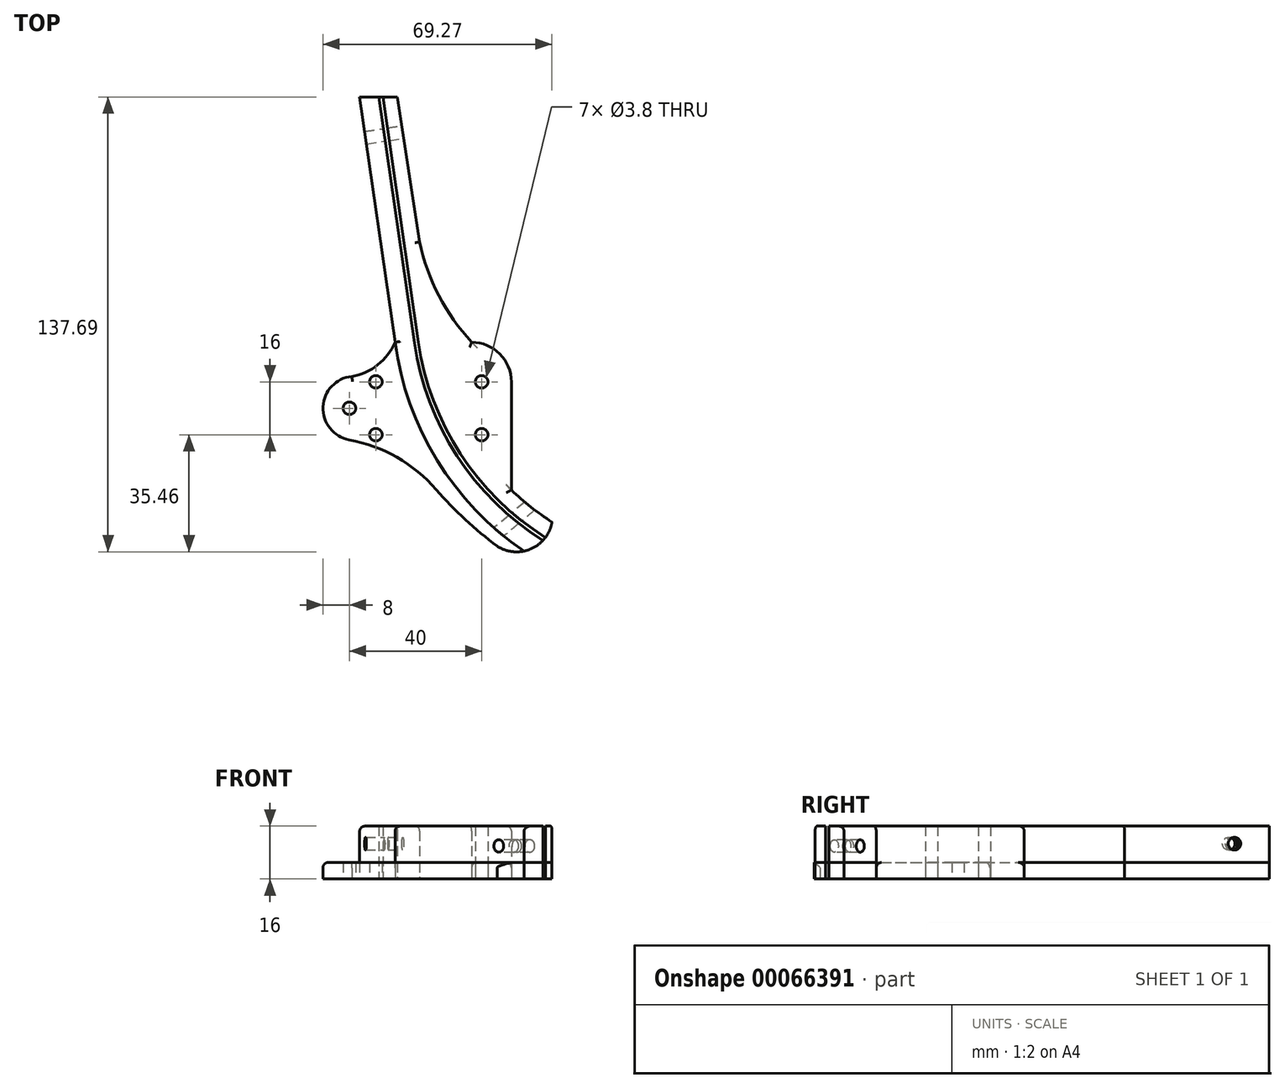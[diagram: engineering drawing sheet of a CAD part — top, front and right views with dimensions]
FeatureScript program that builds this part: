
annotation { "Feature Type Name" : "Feature", "Feature Type Description" : "" }
export const myFeature = defineFeature(function(context is Context, id is Id, definition is map)
    precondition{}
    {
        {
            var Q0;
            Q0=qCreatedBy(makeId("Top.planeOp"),FACE);
            var sketch = newSketch(context, id + "F0", { "sketchPlane" : qUnion([Q0])});
            skLineSegment(sketch, "E0.rect.top", {"start": v(6.92, 32.4) * mm, "end": v(18, 32.4) * mm});
            skLineSegment(sketch, "E0.rect.right", {"start": v(30, -30.94) * mm, "end": v(30, 20.4) * mm});
            skPoint(sketch, "E0.rect.middle", {"position": v(0, 0) * mm});
            skLineSegment(sketch, "E1", {"start": v(0, -32.4) * mm, "end": v(0, -38.4) * mm, "construction": true});
            skPoint(sketch, "E1.endSnap0", {"position": v(0, -32.4) * mm});
            skPoint(sketch, "E2.center", {"position": v(0, 12.4) * mm});
            skLineSegment(sketch, "E3.direction1", {"start": v(8, 12.4) * mm, "end": v(40, 12.4) * mm, "construction": true});
            skLineSegment(sketch, "E4", {"start": v(0, 12.4) * mm, "end": v(85, 12.4) * mm, "construction": true});
            skLineSegment(sketch, "E5", {"start": v(85, 12.4) * mm, "end": v(85, 44.4) * mm, "construction": true});
            skLineSegment(sketch, "E6", {"start": v(0, 12.4) * mm, "end": v(0, 32.4) * mm, "construction": true});
            skLineSegment(sketch, "E7", {"start": v(0, 12.4) * mm, "end": v(0, -32.4) * mm, "construction": true});
            skCircle(sketch, "E8", {"center": v(85, 44.4) * mm, "radius": 11.1 * mm, "construction": true});
            skCircle(sketch, "E9", {"center": v(85, 44.4) * mm, "radius": 80 * mm, "construction": true});
            skArc(sketch, "E10.0", {"start": v(1.86, 32.4) * mm, "mid": v(14.57, -1.37) * mm, "end": v(40.27, -26.7) * mm});
            skArc(sketch, "E11.0", {"start": v(-5.2, 32.4) * mm, "mid": v(7.55, -3.38) * mm, "end": v(33.8, -30.83) * mm});
            skArc(sketch, "E12.0", {"start": v(6.92, 32.4) * mm, "mid": v(18.74, 1.38) * mm, "end": v(42.27, -22.05) * mm});
            skArc(sketch, "E13", {"start": v(-18.28, 22.06) * mm, "mid": v(-27, 12.81) * mm, "end": v(-19.1, 2.86) * mm});
            skArc(sketch, "E14", {"start": v(7.25, -12.26) * mm, "mid": v(16.03, -21.28) * mm, "end": v(25.7, -29.33) * mm});
            skPoint(sketch, "E15.orphan", {"position": v(-30, 32.4) * mm});
            skPoint(sketch, "E16.orphan", {"position": v(-30, -32.4) * mm});
            skLineSegment(sketch, "E17.bottom", {"start": v(30, 32.4) * mm, "end": v(18, 32.4) * mm, "construction": true});
            skLineSegment(sketch, "E17.top", {"start": v(30, 20.4) * mm, "end": v(18, 20.4) * mm, "construction": true});
            skLineSegment(sketch, "E17.left", {"start": v(30, 32.4) * mm, "end": v(30, 20.4) * mm, "construction": true});
            skLineSegment(sketch, "E17.right", {"start": v(18, 32.4) * mm, "end": v(18, 20.4) * mm, "construction": true});
            skArc(sketch, "E18.trimOffspring", {"start": v(30, 20.4) * mm, "mid": v(26.49, 28.89) * mm, "end": v(18, 32.4) * mm});
            skLineSegment(sketch, "E19", {"start": v(85, 12.4) * mm, "end": v(21, 12.4) * mm, "construction": true});
            skLineSegment(sketch, "E20", {"start": v(21, 12.4) * mm, "end": v(21, 20.4) * mm, "construction": true});
            skCircle(sketch, "E21", {"center": v(21, 20.4) * mm, "radius": 1.9 * mm});
            skLineSegment(sketch, "E22", {"start": v(21, 12.4) * mm, "end": v(21, 4.4) * mm, "construction": true});
            skCircle(sketch, "E23", {"center": v(21, 4.4) * mm, "radius": 1.9 * mm});
            skLineSegment(sketch, "E24", {"start": v(21, 12.4) * mm, "end": v(-19, 12.4) * mm, "construction": true});
            skCircle(sketch, "E25", {"center": v(-19, 12.4) * mm, "radius": 1.9 * mm});
            skArc(sketch, "E26", {"start": v(-18.28, 22.06) * mm, "mid": v(-10.43, 25.57) * mm, "end": v(-5.2, 32.4) * mm});
            skArc(sketch, "E27", {"start": v(7.25, -12.26) * mm, "mid": v(-4.62, -2.44) * mm, "end": v(-19.1, 2.86) * mm});
            skLineSegment(sketch, "E28", {"start": v(-11, 12.4) * mm, "end": v(-11, 20.4) * mm, "construction": true});
            skCircle(sketch, "E29", {"center": v(-11, 20.4) * mm, "radius": 1.9 * mm});
            skLineSegment(sketch, "E30", {"start": v(-11, 12.4) * mm, "end": v(-11, 4.4) * mm, "construction": true});
            skCircle(sketch, "E31", {"center": v(-11, 4.4) * mm, "radius": 1.9 * mm});
            skArc(sketch, "E32.0", {"start": v(0.67, 32.23) * mm, "mid": v(13.52, -1.96) * mm, "end": v(39.5, -27.63) * mm});
            skLineSegment(sketch, "E33", {"start": v(0.67, 32.23) * mm, "end": v(0.65, 32.4) * mm});
            skArc(sketch, "E34", {"start": v(25.7, -29.33) * mm, "mid": v(35.94, -30.14) * mm, "end": v(42.27, -22.05) * mm});
            skPoint(sketch, "E35.orphan", {"position": v(30, -32.4) * mm});
            skLineSegment(sketch, "E36", {"start": v(6.92, 32.4) * mm, "end": v(-4.48, 106.53) * mm});
            skLineSegment(sketch, "E37", {"start": v(-5.2, 32.4) * mm, "end": v(-15.92, 106.63) * mm});
            skLineSegment(sketch, "E38", {"start": v(-15.92, 106.63) * mm, "end": v(-4.48, 106.53) * mm});
            skLineSegment(sketch, "E39", {"start": v(0.67, 32.23) * mm, "end": v(-10.06, 106.58) * mm});
            skLineSegment(sketch, "E40", {"start": v(1.86, 32.4) * mm, "end": v(-8.84, 106.57) * mm});
            skArc(sketch, "E41", {"start": v(2.25, 62.76) * mm, "mid": v(8.06, 46.5) * mm, "end": v(18, 32.4) * mm});
            skSolve(sketch);
        }
        {
            var Q0;
            {var subQ0=sQuery(id+"F0.wireOp",EDGE,"E11.0");var subQ5=sQuery(id+"F0.wireOp",EDGE,"E0.rect.right");var subQ6=makeQuery(id+"F0.imprint","INTERSECT",VERTEX,{"derivedFrom":[subQ5,subQ0]});Q0=makeQuery(id+"F0.imprint","IMPRINT",FACE,{"disambiguationData":[TD([[makeQuery(id+"F0.imprint","IMPRINT",EDGE,{"disambiguationData":[TD([[subQ6,-1.0]])],"derivedFrom":subQ5}),1.0]])]});}
            var Q1;
            {var subQ0=sQuery(id+"F0.wireOp",EDGE,"E10.0");var subQ1=sQuery(id+"F0.wireOp",EDGE,"E0.rect.top");var subQ2=makeQuery(id+"F0.imprint","INTERSECT",VERTEX,{"derivedFrom":[subQ1,subQ0]});Q1=makeQuery(id+"F0.imprint","IMPRINT",FACE,{"disambiguationData":[TD([[makeQuery(id+"F0.imprint","IMPRINT",EDGE,{"disambiguationData":[TD([[subQ2,-1.0]])],"derivedFrom":subQ1}),-1.0]])]});}
            var Q2;
            {var subQ0=sQuery(id+"F0.wireOp",EDGE,"E12.0");var subQ1=sQuery(id+"F0.wireOp",EDGE,"E0.rect.right");var subQ2=makeQuery(id+"F0.imprint","INTERSECT",VERTEX,{"derivedFrom":[subQ1,subQ0]});Q2=makeQuery(id+"F0.imprint","IMPRINT",FACE,{"disambiguationData":[TD([[makeQuery(id+"F0.imprint","IMPRINT",EDGE,{"disambiguationData":[TD([[subQ2,1.0]])],"derivedFrom":subQ1}),-1.0]])]});}
            var Q3;
            {var subQ0=sQuery(id+"F0.wireOp",EDGE,"E11.0");var subQ1=sQuery(id+"F0.wireOp",EDGE,"E0.rect.right");var subQ2=makeQuery(id+"F0.imprint","INTERSECT",VERTEX,{"derivedFrom":[subQ1,subQ0]});Q3=makeQuery(id+"F0.imprint","IMPRINT",FACE,{"disambiguationData":[TD([[makeQuery(id+"F0.imprint","IMPRINT",EDGE,{"disambiguationData":[TD([[subQ2,-1.0]])],"derivedFrom":subQ1}),-1.0]])]});}
            var Q4;
            {var subQ0=sQuery(id+"F0.wireOp",EDGE,"E36");Q4=makeQuery(id+"F0.imprint","IMPRINT",FACE,{"disambiguationData":[TD([[makeQuery(id+"F0.imprint","IMPRINT",EDGE,{"derivedFrom":subQ0}),1.0]])]});}
            var Q5;
            {var subQ0=sQuery(id+"F0.wireOp",EDGE,"E0.rect.top");Q5=makeQuery(id+"F0.imprint","IMPRINT",FACE,{"disambiguationData":[TD([[makeQuery(id+"F0.imprint","IMPRINT",EDGE,{"derivedFrom":subQ0}),1.0]])]});}
            extrude(context, id + "F1", {"entities" : qUnion([Q0, Q1, Q2, Q3, Q4, Q5]), "depth" : 16 * mm});
        }
        {
            var Q0;
            Q0 = qSketchRegion(id + "F0", true);
            extrude(context, id + "F2", {"entities" : qUnion([Q0]), "depth" : 5 * mm});
        }
        {
            var Q0;
            Q0=makeQuery(id+"F2.opExtrude","CAP_EDGE",EDGE,{"disambiguationData":[OSD([sQuery(id+"F0.wireOp",EDGE,"E26")])],"isStart":false});
            var Q1;
            Q1=makeQuery(id+"F2.opExtrude","CAP_EDGE",EDGE,{"disambiguationData":[OSD([sQuery(id+"F0.wireOp",EDGE,"E13")])],"isStart":false});
            var Q2;
            Q2=makeQuery(id+"F2.opExtrude","CAP_EDGE",EDGE,{"disambiguationData":[OSD([sQuery(id+"F0.wireOp",EDGE,"E27")])],"isStart":false});
            var Q3;
            Q3=makeQuery(id+"F2.opExtrude","CAP_EDGE",EDGE,{"disambiguationData":[OSD([sQuery(id+"F0.wireOp",EDGE,"E14")])],"isStart":false});
            var Q4;
            Q4=makeQuery(id+"F2.opExtrude","CAP_EDGE",EDGE,{"disambiguationData":[OSD([sQuery(id+"F0.wireOp",EDGE,"E18.trimOffspring")])],"isStart":false});
            var Q5;
            Q5=makeQuery(id+"F1.opExtrude","CAP_EDGE",EDGE,{"disambiguationData":[OSD([sQuery(id+"F0.wireOp",EDGE,"E11.0")])],"isStart":false});
            var Q6;
            Q6=makeQuery(id+"F1.opExtrude","CAP_EDGE",EDGE,{"disambiguationData":[OSD([sQuery(id+"F0.wireOp",EDGE,"E12.0")])],"isStart":false});
            fillet(context, id + "F3", {"entities" : qUnion([Q0, Q1, Q2, Q3, Q4, Q5, Q6]), "radius" : 1.6 * mm, "tangentPropagation" : true, "allowEdgeOverflow" : false});
        }
        {
            var Q0;
            Q0=qCreatedBy(makeId("Front.planeOp"),FACE);
            var sketch = newSketch(context, id + "F4", { "sketchPlane" : qUnion([Q0])});
            skLineSegment(sketch, "E42", {"start": v(0, 98.44) * mm, "end": v(0, -106.52) * mm, "construction": true});
            skSolve(sketch);
        }
        {
            var Q0;
            Q0=qCreatedBy(makeId("Front.planeOp"),FACE);
            var Q1;
            Q1=sQuery(id+"F4.wireOp",EDGE,"E42");
            cPlane(context, id + "F5", {"entities" : qUnion([Q0, Q1]), "cplaneType" : CPlaneType.LINE_ANGLE, "offset" : 150 * mm, "angle" : 50 * degree, "width" : 150 * mm, "height" : 150 * mm});
        }
        {
            var Q0;
            Q0=qCreatedBy(id+"F5.planeOp",FACE);
            cPlane(context, id + "F6", {"entities" : qUnion([Q0]), "cplaneType" : CPlaneType.OFFSET, "offset" : 2 * mm, "width" : 150 * mm, "height" : 150 * mm});
        }
        {
            var Q0;
            Q0=qCreatedBy(id+"F6.planeOp",FACE);
            var sketch = newSketch(context, id + "F7", { "sketchPlane" : qUnion([Q0])});
            skLineSegment(sketch, "E43", {"start": v(0, 0) * mm, "end": v(0, 10) * mm, "construction": true});
            skLineSegment(sketch, "E44", {"start": v(0, 10) * mm, "end": v(18, 10) * mm, "construction": true});
            skLineSegment(sketch, "E45", {"start": v(0, 10) * mm, "end": v(-36, 10) * mm, "construction": true});
            skCircle(sketch, "E46", {"center": v(-36, 10) * mm, "radius": 1.9 * mm});
            skSolve(sketch);
        }
        {
            var Q0;
            Q0=makeQuery(id+"F7.imprint","IMPRINT",FACE,{"disambiguationData":[TD([[makeQuery(id+"F7.imprint","IMPRINT",EDGE,{"derivedFrom":sQuery(id+"F7.wireOp",EDGE,"6c3eabdd-0714-4405-9e84-89e43f334f9b")}),1.0]])]});
            var Q1;
            Q1=makeQuery(id+"F7.imprint","IMPRINT",FACE,{"disambiguationData":[TD([[makeQuery(id+"F7.imprint","IMPRINT",EDGE,{"derivedFrom":sQuery(id+"F7.wireOp",EDGE,"E46")}),1.0]])]});
            extrude(context, id + "F8", {"entities" : qUnion([Q0, Q1]), "operationType" : NewBodyOperationType.REMOVE, "depth" : 25 * mm});
        }
        {
            var Q0;
            Q0=makeQuery(id+"F1.opExtrude","SWEPT_FACE",FACE,{"disambiguationData":[OSD([sQuery(id+"F0.wireOp",EDGE,"E36")])]});
            var sketch = newSketch(context, id + "F9", { "sketchPlane" : qUnion([Q0])});
            skLineSegment(sketch, "E47", {"start": v(105.97, 10.68) * mm, "end": v(30.97, 10.68) * mm, "construction": true});
            skCircle(sketch, "E48", {"center": v(95.33, 10.68) * mm, "radius": 1.93 * mm});
            skSolve(sketch);
        }
        {
            var Q0;
            Q0=makeQuery(id+"F9.imprint","IMPRINT",FACE,{"disambiguationData":[TD([[makeQuery(id+"F9.imprint","IMPRINT",EDGE,{"derivedFrom":sQuery(id+"F9.wireOp",EDGE,"E48")}),1.0]])]});
            extrude(context, id + "F10", {"entities" : qUnion([Q0]), "operationType" : NewBodyOperationType.REMOVE, "endBound" : BoundingType.THROUGH_ALL, "oppositeDirection" : true, "depth" : 100 * mm});
        }
        {
            var Q0;
            Q0=makeQuery(id+"F1.opExtrude","CAP_EDGE",EDGE,{"disambiguationData":[OSD([sQuery(id+"F0.wireOp",EDGE,"E36")])],"isStart":false});
            var Q1;
            Q1=makeQuery(id+"F1.opExtrude","CAP_EDGE",EDGE,{"disambiguationData":[OSD([sQuery(id+"F0.wireOp",EDGE,"E18.trimOffspring")])],"isStart":false});
            fillet(context, id + "F11", {"entities" : qUnion([Q0, Q1]), "radius" : 1.5 * mm, "tangentPropagation" : true, "allowEdgeOverflow" : false});
        }
    });
